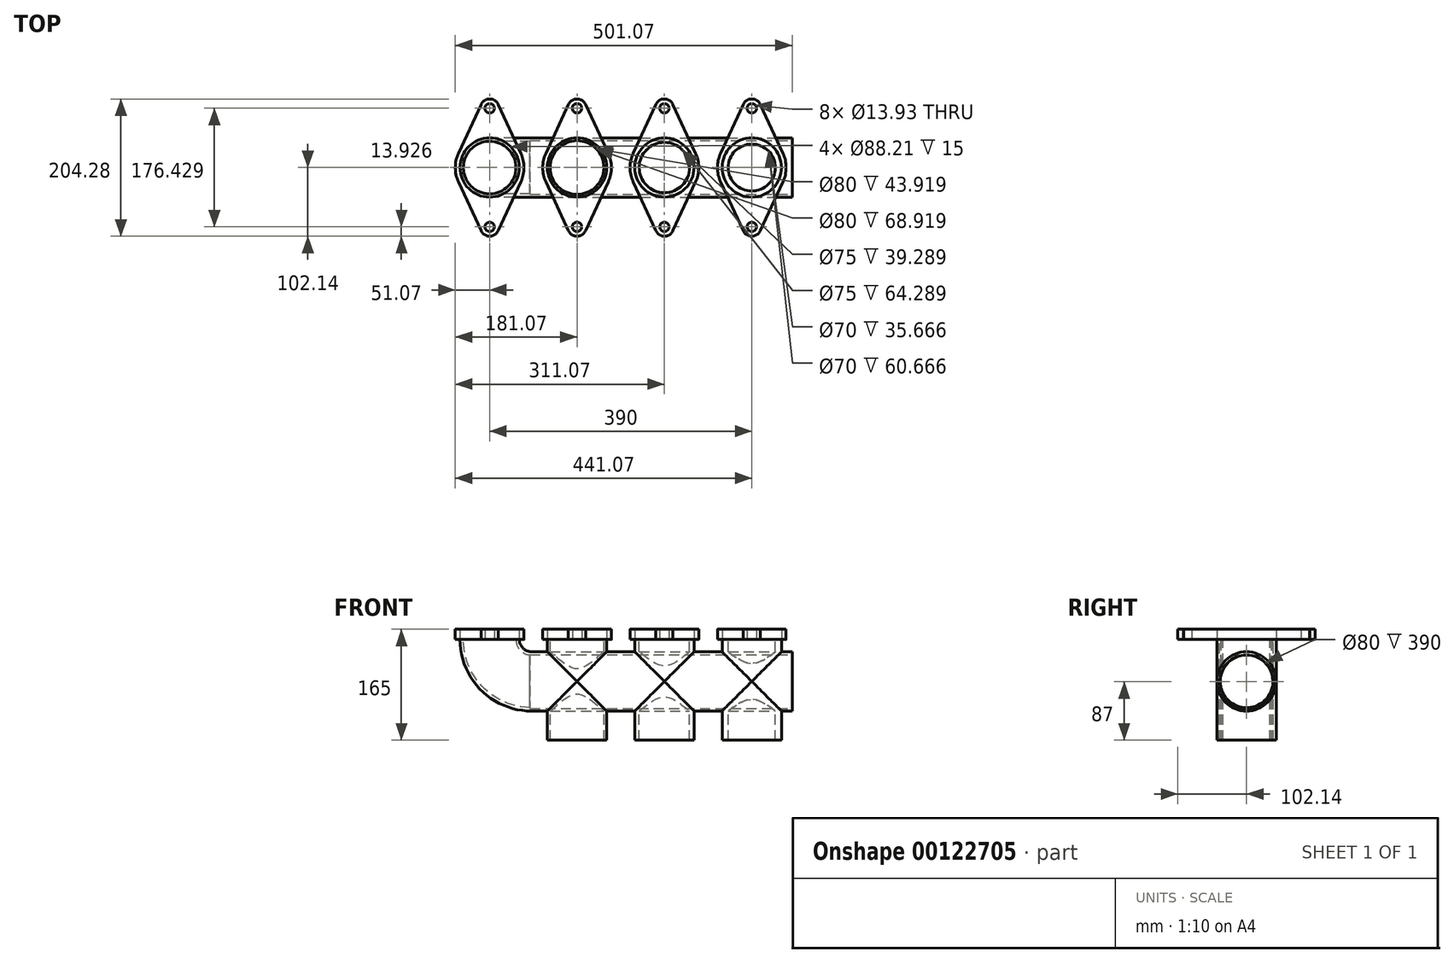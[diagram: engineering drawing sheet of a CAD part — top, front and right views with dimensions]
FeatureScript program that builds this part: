
annotation { "Feature Type Name" : "Feature", "Feature Type Description" : "" }
export const myFeature = defineFeature(function(context is Context, id is Id, definition is map)
    precondition{}
    {
        {
            var Q0;
            Q0=qCreatedBy(makeId("Front.planeOp"),FACE);
            var sketch = newSketch(context, id + "F0", { "sketchPlane" : qUnion([Q0])});
            skArc(sketch, "E0", {"start": v(0, 0) * mm, "mid": v(18.3, -44.2) * mm, "end": v(62.5, -62.5) * mm});
            skLineSegment(sketch, "E1", {"start": v(62.5, -62.5) * mm, "end": v(450, -62.5) * mm});
            skSolve(sketch);
        }
        {
            var Q0;
            Q0=qCreatedBy(makeId("Top.planeOp"),FACE);
            var sketch = newSketch(context, id + "F1", { "sketchPlane" : qUnion([Q0])});
            skCircle(sketch, "E2", {"center": v(0, 0) * mm, "radius": 44.1 * mm});
            skArc(sketch, "E3", {"start": v(-46.32, 21.5) * mm, "mid": v(-51.07, 0) * mm, "end": v(-46.32, -21.5) * mm});
            skLineSegment(sketch, "E4", {"start": v(0, 0) * mm, "end": v(101.04, 0) * mm});
            skLineSegment(sketch, "E5", {"start": v(0, 0) * mm, "end": v(0, 88.21) * mm});
            skArc(sketch, "E6", {"start": v(12.79, 93.74) * mm, "mid": v(0, 102.14) * mm, "end": v(-12.79, 93.74) * mm});
            skCircle(sketch, "E7", {"center": v(0, 88.21) * mm, "radius": 6.96 * mm});
            skLineSegment(sketch, "E8", {"start": v(-12.79, 93.74) * mm, "end": v(-46.32, 21.5) * mm});
            skLineSegment(sketch, "E9.MirrorCS", {"start": v(12.79, 93.74) * mm, "end": v(46.32, 21.5) * mm});
            skLineSegment(sketch, "E10.MirrorCS", {"start": v(12.79, -93.74) * mm, "end": v(46.32, -21.5) * mm});
            skArc(sketch, "E11.MirrorCS", {"start": v(12.79, -93.74) * mm, "mid": v(0, -102.14) * mm, "end": v(-12.79, -93.74) * mm});
            skLineSegment(sketch, "E12.MirrorCS", {"start": v(-12.79, -93.74) * mm, "end": v(-46.32, -21.5) * mm});
            skArc(sketch, "E13.trimOffspring", {"start": v(46.32, -21.5) * mm, "mid": v(51.07, 0) * mm, "end": v(46.32, 21.5) * mm});
            skCircle(sketch, "E14.MirrorC", {"center": v(0, -88.21) * mm, "radius": 6.96 * mm});
            skLineSegment(sketch, "E15.1.0.0", {"start": v(117.21, 93.74) * mm, "end": v(83.68, 21.5) * mm});
            skArc(sketch, "E15.1.0.1", {"start": v(83.68, 21.5) * mm, "mid": v(78.93, 0) * mm, "end": v(83.68, -21.5) * mm});
            skLineSegment(sketch, "E15.1.0.2", {"start": v(142.79, -93.74) * mm, "end": v(176.32, -21.5) * mm});
            skLineSegment(sketch, "E15.1.0.3", {"start": v(142.79, 93.74) * mm, "end": v(176.32, 21.5) * mm});
            skCircle(sketch, "E15.1.0.4", {"center": v(130, 0) * mm, "radius": 44.1 * mm});
            skArc(sketch, "E15.1.0.5", {"start": v(142.79, 93.74) * mm, "mid": v(130, 102.14) * mm, "end": v(117.21, 93.74) * mm});
            skArc(sketch, "E15.1.0.6", {"start": v(176.32, -21.5) * mm, "mid": v(181.07, 0) * mm, "end": v(176.32, 21.5) * mm});
            skLineSegment(sketch, "E15.1.0.7", {"start": v(117.21, -93.74) * mm, "end": v(83.68, -21.5) * mm});
            skArc(sketch, "E15.1.0.8", {"start": v(142.79, -93.74) * mm, "mid": v(130, -102.14) * mm, "end": v(117.21, -93.74) * mm});
            skCircle(sketch, "E15.1.0.9", {"center": v(130, -88.21) * mm, "radius": 6.96 * mm});
            skCircle(sketch, "E15.1.0.10", {"center": v(130, 88.21) * mm, "radius": 6.96 * mm});
            skLineSegment(sketch, "E15.2.0.0", {"start": v(247.21, 93.74) * mm, "end": v(213.68, 21.5) * mm});
            skArc(sketch, "E15.2.0.1", {"start": v(213.68, 21.5) * mm, "mid": v(208.93, 0) * mm, "end": v(213.68, -21.5) * mm});
            skLineSegment(sketch, "E15.2.0.2", {"start": v(272.79, -93.74) * mm, "end": v(306.32, -21.5) * mm});
            skLineSegment(sketch, "E15.2.0.3", {"start": v(272.79, 93.74) * mm, "end": v(306.32, 21.5) * mm});
            skCircle(sketch, "E15.2.0.4", {"center": v(260, 0) * mm, "radius": 44.1 * mm});
            skArc(sketch, "E15.2.0.5", {"start": v(272.79, 93.74) * mm, "mid": v(260, 102.14) * mm, "end": v(247.21, 93.74) * mm});
            skArc(sketch, "E15.2.0.6", {"start": v(306.32, -21.5) * mm, "mid": v(311.07, 0) * mm, "end": v(306.32, 21.5) * mm});
            skLineSegment(sketch, "E15.2.0.7", {"start": v(247.21, -93.74) * mm, "end": v(213.68, -21.5) * mm});
            skArc(sketch, "E15.2.0.8", {"start": v(272.79, -93.74) * mm, "mid": v(260, -102.14) * mm, "end": v(247.21, -93.74) * mm});
            skCircle(sketch, "E15.2.0.9", {"center": v(260, -88.21) * mm, "radius": 6.96 * mm});
            skCircle(sketch, "E15.2.0.10", {"center": v(260, 88.21) * mm, "radius": 6.96 * mm});
            skLineSegment(sketch, "E15.3.0.0", {"start": v(377.21, 93.74) * mm, "end": v(343.68, 21.5) * mm});
            skArc(sketch, "E15.3.0.1", {"start": v(343.68, 21.5) * mm, "mid": v(338.93, 0) * mm, "end": v(343.68, -21.5) * mm});
            skLineSegment(sketch, "E15.3.0.2", {"start": v(402.79, -93.74) * mm, "end": v(436.32, -21.5) * mm});
            skLineSegment(sketch, "E15.3.0.3", {"start": v(402.79, 93.74) * mm, "end": v(436.32, 21.5) * mm});
            skCircle(sketch, "E15.3.0.4", {"center": v(390, 0) * mm, "radius": 44.1 * mm});
            skArc(sketch, "E15.3.0.5", {"start": v(402.79, 93.74) * mm, "mid": v(390, 102.14) * mm, "end": v(377.21, 93.74) * mm});
            skArc(sketch, "E15.3.0.6", {"start": v(436.32, -21.5) * mm, "mid": v(441.07, 0) * mm, "end": v(436.32, 21.5) * mm});
            skLineSegment(sketch, "E15.3.0.7", {"start": v(377.21, -93.74) * mm, "end": v(343.68, -21.5) * mm});
            skArc(sketch, "E15.3.0.8", {"start": v(402.79, -93.74) * mm, "mid": v(390, -102.14) * mm, "end": v(377.21, -93.74) * mm});
            skCircle(sketch, "E15.3.0.9", {"center": v(390, -88.21) * mm, "radius": 6.96 * mm});
            skCircle(sketch, "E15.3.0.10", {"center": v(390, 88.21) * mm, "radius": 6.96 * mm});
            skLineSegment(sketch, "E15.direction1", {"start": v(-12.79, -93.74) * mm, "end": v(117.21, -93.74) * mm, "construction": true});
            skCircle(sketch, "E16", {"center": v(130, 0) * mm, "radius": 40 * mm});
            skCircle(sketch, "E17", {"center": v(260, 0) * mm, "radius": 37.5 * mm});
            skCircle(sketch, "E18", {"center": v(390, 0) * mm, "radius": 35 * mm});
            skSolve(sketch);
        }
        {
            var Q0;
            Q0=qCreatedBy(makeId("Right.planeOp"),FACE);
            cPlane(context, id + "F2", {"entities" : qUnion([Q0]), "cplaneType" : CPlaneType.OFFSET, "offset" : 450 * mm, "width" : 150 * mm, "height" : 150 * mm});
        }
        {
            var Q0;
            Q0=qCreatedBy(id+"F2.planeOp",FACE);
            var sketch = newSketch(context, id + "F3", { "sketchPlane" : qUnion([Q0])});
            skCircle(sketch, "E19", {"center": v(0, -63) * mm, "radius": 47.5 * mm});
            skCircle(sketch, "E20", {"center": v(0, -63) * mm, "radius": 40 * mm});
            skSolve(sketch);
        }
        {
            var Q0;
            Q0=makeQuery(id+"F1.imprint","IMPRINT",FACE,{"disambiguationData":[TD([[makeQuery(id+"F1.imprint","IMPRINT",EDGE,{"derivedFrom":sQuery(id+"F1.wireOp",EDGE,"E2")}),1.0]])]});
            var Q1;
            Q1=sQuery(id+"F0.wireOp",EDGE,"E0");
            var Q2;
            Q2=sQuery(id+"F0.wireOp",EDGE,"E1");
            sweep(context, id + "F4", {"profiles" : qUnion([Q0]), "path" : qUnion([Q1, Q2])});
        }
        {
            var Q0;
            Q0=makeQuery(id+"F4.opSweep","CAP_FACE",FACE,{"disambiguationData":[OSD([sQuery(id+"F0.wireOp",VERTEX,"E0.start"),sQuery(id+"F1.wireOp",EDGE,"E2")])],"isStart":true});
            var Q1;
            Q1=makeQuery(id+"F4.opSweep","CAP_FACE",FACE,{"disambiguationData":[OSD([sQuery(id+"F0.wireOp",VERTEX,"E1.end"),sQuery(id+"F1.wireOp",EDGE,"E2")])],"isStart":false});
            shell(context, id + "F5", {"entities" : qUnion([Q0, Q1]), "thickness" : 5 * mm});
        }
        {
            var Q0;
            Q0=sQuery(id+"F1.wireOp",EDGE,"E15.1.0.4");
            var Q1;
            Q1=sQuery(id+"F1.wireOp",EDGE,"E16");
            var Q2;
            Q2=sQuery(id+"F1.wireOp",EDGE,"E17");
            var Q3;
            Q3=sQuery(id+"F1.wireOp",EDGE,"E15.2.0.4");
            var Q4;
            Q4=sQuery(id+"F1.wireOp",EDGE,"E15.3.0.4");
            var Q5;
            Q5=sQuery(id+"F1.wireOp",EDGE,"E18");
            extrude(context, id + "F6", {"bodyType" : ToolBodyType.SURFACE, "surfaceEntities" : qUnion([Q0, Q1, Q2, Q3, Q4, Q5]), "oppositeDirection" : true, "depth" : 62 * mm});
        }
        {
            var Q0;
            Q0=makeQuery(id+"F1.imprint","IMPRINT",FACE,{"disambiguationData":[TD([[makeQuery(id+"F1.imprint","IMPRINT",EDGE,{"derivedFrom":sQuery(id+"F1.wireOp",EDGE,"E3")}),1.0]])]});
            var Q1;
            {var subQ3=sQuery(id+"F1.wireOp",EDGE,"E15.1.0.0");Q1=makeQuery(id+"F1.imprint","IMPRINT",FACE,{"disambiguationData":[TD([[makeQuery(id+"F1.imprint","IMPRINT",EDGE,{"derivedFrom":subQ3}),1.0]])]});}
            var Q2;
            Q2=makeQuery(id+"F1.imprint","IMPRINT",FACE,{"disambiguationData":[TD([[makeQuery(id+"F1.imprint","IMPRINT",EDGE,{"derivedFrom":sQuery(id+"F1.wireOp",EDGE,"E15.2.0.0")}),1.0]])]});
            var Q3;
            Q3=makeQuery(id+"F1.imprint","IMPRINT",FACE,{"disambiguationData":[TD([[makeQuery(id+"F1.imprint","IMPRINT",EDGE,{"derivedFrom":sQuery(id+"F1.wireOp",EDGE,"E15.3.0.0")}),1.0]])]});
            extrude(context, id + "F7", {"entities" : qUnion([Q0, Q1, Q2, Q3]), "depth" : 15 * mm});
        }
        {
            var Q0;
            Q0=makeQuery(id+"F1.imprint","IMPRINT",FACE,{"disambiguationData":[TD([[makeQuery(id+"F1.imprint","IMPRINT",EDGE,{"derivedFrom":sQuery(id+"F1.wireOp",EDGE,"E15.1.0.4")}),1.0]])]});
            var Q1;
            Q1=makeQuery(id+"F1.imprint","IMPRINT",FACE,{"disambiguationData":[TD([[makeQuery(id+"F1.imprint","IMPRINT",EDGE,{"derivedFrom":sQuery(id+"F1.wireOp",EDGE,"E15.2.0.4")}),1.0]])]});
            var Q2;
            Q2=makeQuery(id+"F1.imprint","IMPRINT",FACE,{"disambiguationData":[TD([[makeQuery(id+"F1.imprint","IMPRINT",EDGE,{"derivedFrom":sQuery(id+"F1.wireOp",EDGE,"E15.3.0.4")}),1.0]])]});
            extrude(context, id + "F8", {"entities" : qUnion([Q0, Q1, Q2]), "operationType" : NewBodyOperationType.ADD, "oppositeDirection" : true, "depth" : 150 * mm});
        }
        {
            var Q0;
            Q0=makeQuery(id+"F3.imprint","IMPRINT",FACE,{"disambiguationData":[TD([[makeQuery(id+"F3.imprint","IMPRINT",EDGE,{"derivedFrom":sQuery(id+"F3.wireOp",EDGE,"E20")}),1.0]])]});
            extrude(context, id + "F9", {"entities" : qUnion([Q0]), "operationType" : NewBodyOperationType.REMOVE, "oppositeDirection" : true, "depth" : 390 * mm});
        }
    });
